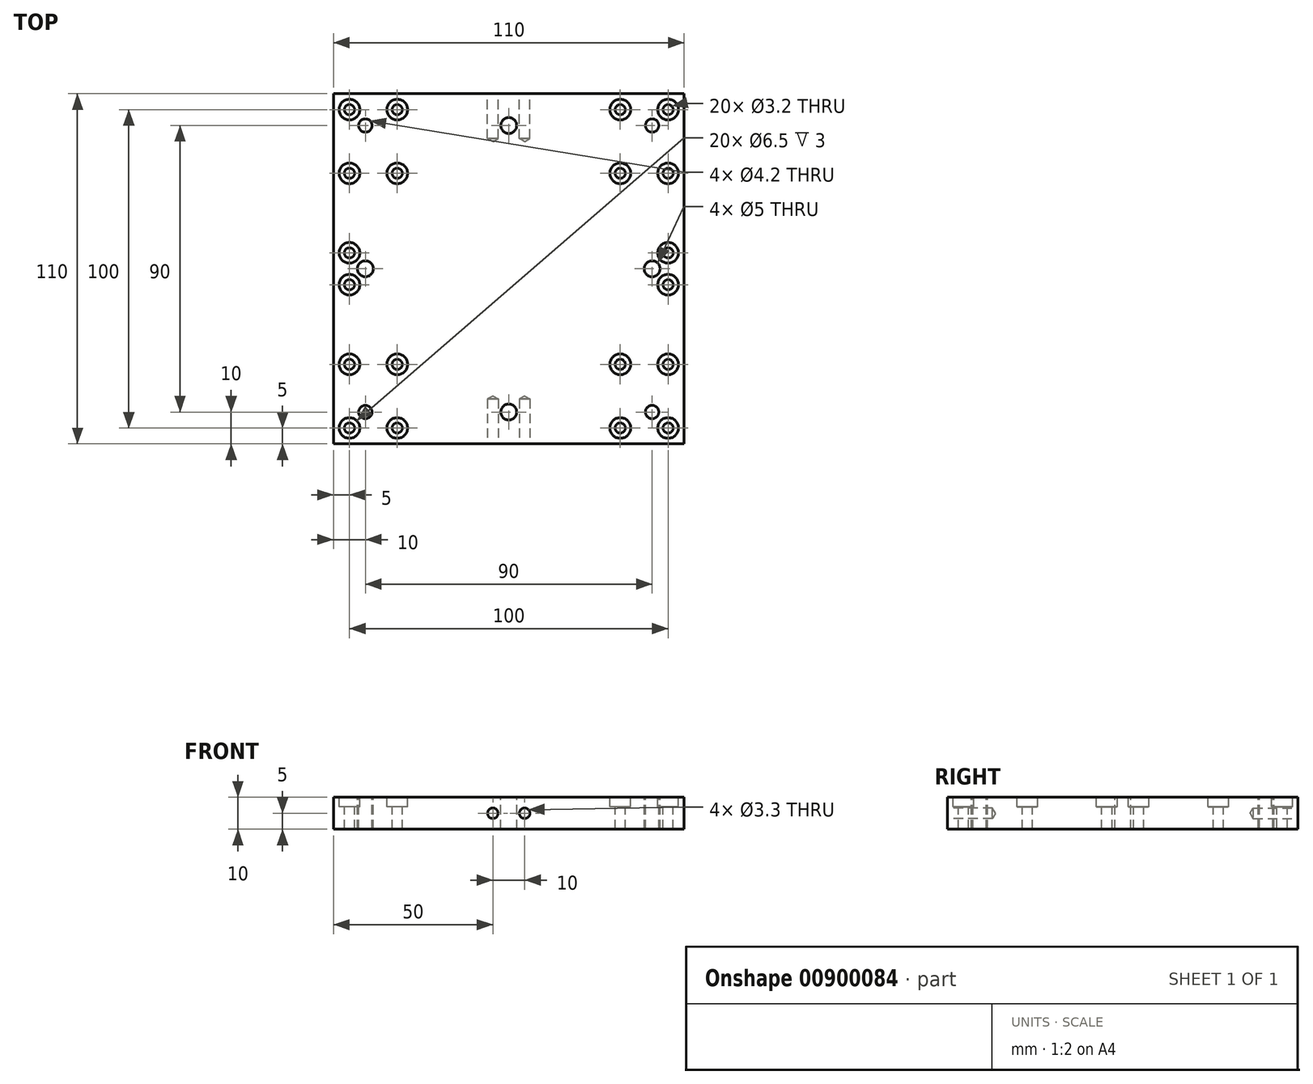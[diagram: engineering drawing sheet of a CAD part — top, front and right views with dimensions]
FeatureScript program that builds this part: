
annotation { "Feature Type Name" : "Feature", "Feature Type Description" : "" }
export const myFeature = defineFeature(function(context is Context, id is Id, definition is map)
    precondition{}
    {
        {
            var Q0;
            Q0=qCreatedBy(makeId("Top.planeOp"),FACE);
            var sketch = newSketch(context, id + "F0", { "sketchPlane" : qUnion([Q0])});
            skLineSegment(sketch, "E0.bottom", {"start": v(55, -55) * mm, "end": v(-55, -55) * mm});
            skLineSegment(sketch, "E0.top", {"start": v(55, 55) * mm, "end": v(-55, 55) * mm});
            skLineSegment(sketch, "E0.left", {"start": v(55, -55) * mm, "end": v(55, 55) * mm});
            skLineSegment(sketch, "E0.right", {"start": v(-55, -55) * mm, "end": v(-55, 55) * mm});
            skPoint(sketch, "E0.middle", {"position": v(0, 0) * mm});
            skLineSegment(sketch, "E1.bottom", {"start": v(45, -45) * mm, "end": v(-45, -45) * mm, "construction": true});
            skLineSegment(sketch, "E1.top", {"start": v(45, 45) * mm, "end": v(-45, 45) * mm, "construction": true});
            skLineSegment(sketch, "E1.left", {"start": v(45, -45) * mm, "end": v(45, 45) * mm, "construction": true});
            skLineSegment(sketch, "E1.right", {"start": v(-45, -45) * mm, "end": v(-45, 45) * mm, "construction": true});
            skPoint(sketch, "E2", {"position": v(0, -45) * mm});
            skPoint(sketch, "E3", {"position": v(0, 45) * mm});
            skPoint(sketch, "E4", {"position": v(-45, 0) * mm});
            skPoint(sketch, "E5", {"position": v(45, 0) * mm});
            skLineSegment(sketch, "E6.bottom", {"start": v(50, -5) * mm, "end": v(-50, -5) * mm, "construction": true});
            skLineSegment(sketch, "E6.top", {"start": v(50, 5) * mm, "end": v(-50, 5) * mm, "construction": true});
            skLineSegment(sketch, "E6.left", {"start": v(50, -5) * mm, "end": v(50, 5) * mm, "construction": true});
            skLineSegment(sketch, "E6.right", {"start": v(-50, -5) * mm, "end": v(-50, 5) * mm, "construction": true});
            skLineSegment(sketch, "E7.bottom", {"start": v(-50, -50) * mm, "end": v(-35, -50) * mm, "construction": true});
            skLineSegment(sketch, "E7.top", {"start": v(-50, -30) * mm, "end": v(-35, -30) * mm, "construction": true});
            skLineSegment(sketch, "E7.left", {"start": v(-50, -50) * mm, "end": v(-50, -30) * mm, "construction": true});
            skLineSegment(sketch, "E7.right", {"start": v(-35, -50) * mm, "end": v(-35, -30) * mm, "construction": true});
            skPoint(sketch, "E7.middle", {"position": v(-42.5, -40) * mm});
            skLineSegment(sketch, "E8.bottom", {"start": v(50, -50) * mm, "end": v(35, -50) * mm, "construction": true});
            skLineSegment(sketch, "E8.top", {"start": v(50, -30) * mm, "end": v(35, -30) * mm, "construction": true});
            skLineSegment(sketch, "E8.left", {"start": v(50, -50) * mm, "end": v(50, -30) * mm, "construction": true});
            skLineSegment(sketch, "E8.right", {"start": v(35, -50) * mm, "end": v(35, -30) * mm, "construction": true});
            skLineSegment(sketch, "E9.bottom", {"start": v(-50, 50) * mm, "end": v(-35, 50) * mm, "construction": true});
            skLineSegment(sketch, "E9.top", {"start": v(-50, 30) * mm, "end": v(-35, 30) * mm, "construction": true});
            skLineSegment(sketch, "E9.left", {"start": v(-50, 50) * mm, "end": v(-50, 30) * mm, "construction": true});
            skLineSegment(sketch, "E9.right", {"start": v(-35, 50) * mm, "end": v(-35, 30) * mm, "construction": true});
            skLineSegment(sketch, "E10.bottom", {"start": v(50, 50) * mm, "end": v(35, 50) * mm, "construction": true});
            skLineSegment(sketch, "E10.top", {"start": v(50, 30) * mm, "end": v(35, 30) * mm, "construction": true});
            skLineSegment(sketch, "E10.left", {"start": v(50, 50) * mm, "end": v(50, 30) * mm, "construction": true});
            skLineSegment(sketch, "E10.right", {"start": v(35, 50) * mm, "end": v(35, 30) * mm, "construction": true});
            skSolve(sketch);
        }
        {
            var Q0;
            Q0=makeQuery(id+"F0.imprint","IMPRINT",FACE,{"disambiguationData":[TD([[makeQuery(id+"F0.imprint","IMPRINT",EDGE,{"derivedFrom":sQuery(id+"F0.wireOp",EDGE,"E0.bottom")}),-1.0]])]});
            extrude(context, id + "F1", {"entities" : qUnion([Q0]), "oppositeDirection" : true, "depth" : 10 * mm, "offsetDistance" : 25 * mm});
        }
        {
            var Q0;
            Q0=sQuery(id+"F0.wireOp",VERTEX,"E9.top.start");
            var Q1;
            Q1=sQuery(id+"F0.wireOp",VERTEX,"E9.top.end");
            var Q2;
            Q2=sQuery(id+"F0.wireOp",VERTEX,"E9.bottom.end");
            var Q3;
            Q3=sQuery(id+"F0.wireOp",VERTEX,"E9.bottom.start");
            var Q4;
            Q4=sQuery(id+"F0.wireOp",VERTEX,"E7.top.start");
            var Q5;
            Q5=sQuery(id+"F0.wireOp",VERTEX,"E7.top.end");
            var Q6;
            Q6=sQuery(id+"F0.wireOp",VERTEX,"E7.bottom.end");
            var Q7;
            Q7=sQuery(id+"F0.wireOp",VERTEX,"E7.bottom.start");
            var Q8;
            Q8=sQuery(id+"F0.wireOp",VERTEX,"E8.top.end");
            var Q9;
            Q9=sQuery(id+"F0.wireOp",VERTEX,"E8.bottom.end");
            var Q10;
            Q10=sQuery(id+"F0.wireOp",VERTEX,"E8.bottom.start");
            var Q11;
            Q11=sQuery(id+"F0.wireOp",VERTEX,"E8.top.start");
            var Q12;
            Q12=sQuery(id+"F0.wireOp",VERTEX,"E10.top.end");
            var Q13;
            Q13=sQuery(id+"F0.wireOp",VERTEX,"E10.bottom.end");
            var Q14;
            Q14=sQuery(id+"F0.wireOp",VERTEX,"E10.bottom.start");
            var Q15;
            Q15=sQuery(id+"F0.wireOp",VERTEX,"E10.top.start");
            var Q16;
            Q16=sQuery(id+"F0.wireOp",VERTEX,"E6.top.end");
            var Q17;
            Q17=sQuery(id+"F0.wireOp",VERTEX,"E6.bottom.end");
            var Q18;
            Q18=sQuery(id+"F0.wireOp",VERTEX,"E6.top.start");
            var Q19;
            Q19=sQuery(id+"F0.wireOp",VERTEX,"E6.bottom.start");
            var Q20;
            Q20=makeQuery(id+"F1.opExtrude","SWEPT_BODY",BODY,{"disambiguationData":[OSD([sQuery(id+"F0.wireOp",EDGE,"E0.bottom"),sQuery(id+"F0.wireOp",EDGE,"E0.top"),sQuery(id+"F0.wireOp",EDGE,"E0.left"),sQuery(id+"F0.wireOp",EDGE,"E0.right")])]});
            hole(context, id + "F2", {"style" : HoleStyle.C_BORE, "endStyle" : HoleEndStyle.THROUGH, "standardTappedOrClearance" : lookupTablePath({ "fit" : "Close", "standard" : "ISO", "size" : "M3", "type" : "Clearance" }), "standardBlindInLast" : lookupTablePath({ "fit" : "Close", "standard" : "ISO", "size" : "M3", "type" : "Clearance" }), "holeDiameter" : 3.2 * mm, "cBoreDiameter" : 6.5 * mm, "cBoreDepth" : 3 * mm, "majorDiameter" : 3 * mm, "tappedDepth" : 12 * mm, "tapClearance" : 3, "startFromSketch" : true, "locations" : qUnion([Q0, Q1, Q2, Q3, Q4, Q5, Q6, Q7, Q8, Q9, Q10, Q11, Q12, Q13, Q14, Q15, Q16, Q17, Q18, Q19]), "scope" : qUnion([Q20])});
        }
        {
            var Q0;
            Q0=sQuery(id+"F0.wireOp",VERTEX,"E1.top.end");
            var Q1;
            Q1=sQuery(id+"F0.wireOp",VERTEX,"E1.top.start");
            var Q2;
            Q2=sQuery(id+"F0.wireOp",VERTEX,"E1.bottom.start");
            var Q3;
            Q3=sQuery(id+"F0.wireOp",VERTEX,"E1.bottom.end");
            var Q4;
            Q4=makeQuery(id+"F1.opExtrude","SWEPT_BODY",BODY,{"disambiguationData":[OSD([sQuery(id+"F0.wireOp",EDGE,"E0.bottom"),sQuery(id+"F0.wireOp",EDGE,"E0.top"),sQuery(id+"F0.wireOp",EDGE,"E0.left"),sQuery(id+"F0.wireOp",EDGE,"E0.right")])]});
            hole(context, id + "F3", {"style" : HoleStyle.SIMPLE, "endStyle" : HoleEndStyle.THROUGH, "standardTappedOrClearance" : lookupTablePath({ "standard" : "ISO", "engagement" : "75%", "pitch" : "0.8 mm", "size" : "M5", "type" : "Tapped" }), "standardBlindInLast" : lookupTablePath({ "standard" : "ISO", "engagement" : "75%", "pitch" : "0.8 mm", "size" : "M5", "type" : "Tapped" }), "holeDiameter" : 4.2 * mm, "majorDiameter" : 5 * mm, "showTappedDepth" : true, "tappedDepth" : 12 * mm, "tapClearance" : 3, "startFromSketch" : true, "locations" : qUnion([Q0, Q1, Q2, Q3]), "scope" : qUnion([Q4])});
        }
        {
            var Q0;
            Q0=makeQuery(id+"F1.opExtrude","SWEPT_FACE",FACE,{"disambiguationData":[OSD([sQuery(id+"F0.wireOp",EDGE,"E0.bottom")])]});
            var sketch = newSketch(context, id + "F4", { "sketchPlane" : qUnion([Q0])});
            skLineSegment(sketch, "E11", {"start": v(-5, -5) * mm, "end": v(5, -5) * mm});
            skSolve(sketch);
        }
        {
            var Q0;
            Q0=makeQuery(id+"F1.opExtrude","SWEPT_FACE",FACE,{"disambiguationData":[OSD([sQuery(id+"F0.wireOp",EDGE,"E0.top")])]});
            var sketch = newSketch(context, id + "F5", { "sketchPlane" : qUnion([Q0])});
            skLineSegment(sketch, "E12.0", {"start": v(5, -5) * mm, "end": v(-5, -5) * mm});
            skSolve(sketch);
        }
        {
            var Q0;
            Q0=sQuery(id+"F5.wireOp",VERTEX,"E12.0.end");
            var Q1;
            Q1=sQuery(id+"F5.wireOp",VERTEX,"E12.0.start");
            var Q2;
            Q2=sQuery(id+"F4.wireOp",VERTEX,"E11.start");
            var Q3;
            Q3=sQuery(id+"F4.wireOp",VERTEX,"E11.end");
            var Q4;
            Q4=makeQuery(id+"F1.opExtrude","SWEPT_BODY",BODY,{"disambiguationData":[OSD([sQuery(id+"F0.wireOp",EDGE,"E0.bottom"),sQuery(id+"F0.wireOp",EDGE,"E0.top"),sQuery(id+"F0.wireOp",EDGE,"E0.left"),sQuery(id+"F0.wireOp",EDGE,"E0.right")])]});
            hole(context, id + "F6", {"style" : HoleStyle.SIMPLE, "endStyle" : HoleEndStyle.BLIND, "standardTappedOrClearance" : lookupTablePath({ "standard" : "ISO", "engagement" : "75%", "pitch" : "0.7 mm", "size" : "M4", "type" : "Tapped" }), "standardBlindInLast" : lookupTablePath({ "standard" : "ISO", "engagement" : "75%", "pitch" : "0.7 mm", "size" : "M4", "type" : "Tapped" }), "holeDiameter" : 3.3 * mm, "majorDiameter" : 4 * mm, "showTappedDepth" : true, "holeDepth" : 14.1 * mm, "tappedDepth" : 12 * mm, "tapClearance" : 3, "startFromSketch" : true, "locations" : qUnion([Q0, Q1, Q2, Q3]), "scope" : qUnion([Q4])});
        }
        {
            var Q0;
            Q0=sQuery(id+"F0.wireOp",VERTEX,"E2");
            var Q1;
            Q1=sQuery(id+"F0.wireOp",VERTEX,"E5");
            var Q2;
            Q2=sQuery(id+"F0.wireOp",VERTEX,"E3");
            var Q3;
            Q3=sQuery(id+"F0.wireOp",VERTEX,"E4");
            var Q4;
            Q4=makeQuery(id+"F1.opExtrude","SWEPT_BODY",BODY,{"disambiguationData":[OSD([sQuery(id+"F0.wireOp",EDGE,"E0.bottom"),sQuery(id+"F0.wireOp",EDGE,"E0.top"),sQuery(id+"F0.wireOp",EDGE,"E0.left"),sQuery(id+"F0.wireOp",EDGE,"E0.right")])]});
            hole(context, id + "F7", {"style" : HoleStyle.SIMPLE, "endStyle" : HoleEndStyle.THROUGH, "standardTappedOrClearance" : lookupTablePath({ "standard" : "ISO", "size" : "5", "type" : "Drilled" }), "standardBlindInLast" : lookupTablePath({ "standard" : "ISO", "size" : "5", "type" : "Drilled" }), "holeDiameter" : 5 * mm, "majorDiameter" : 5 * mm, "tappedDepth" : 12 * mm, "tapClearance" : 3, "startFromSketch" : true, "locations" : qUnion([Q0, Q1, Q2, Q3]), "scope" : qUnion([Q4])});
        }
    });
